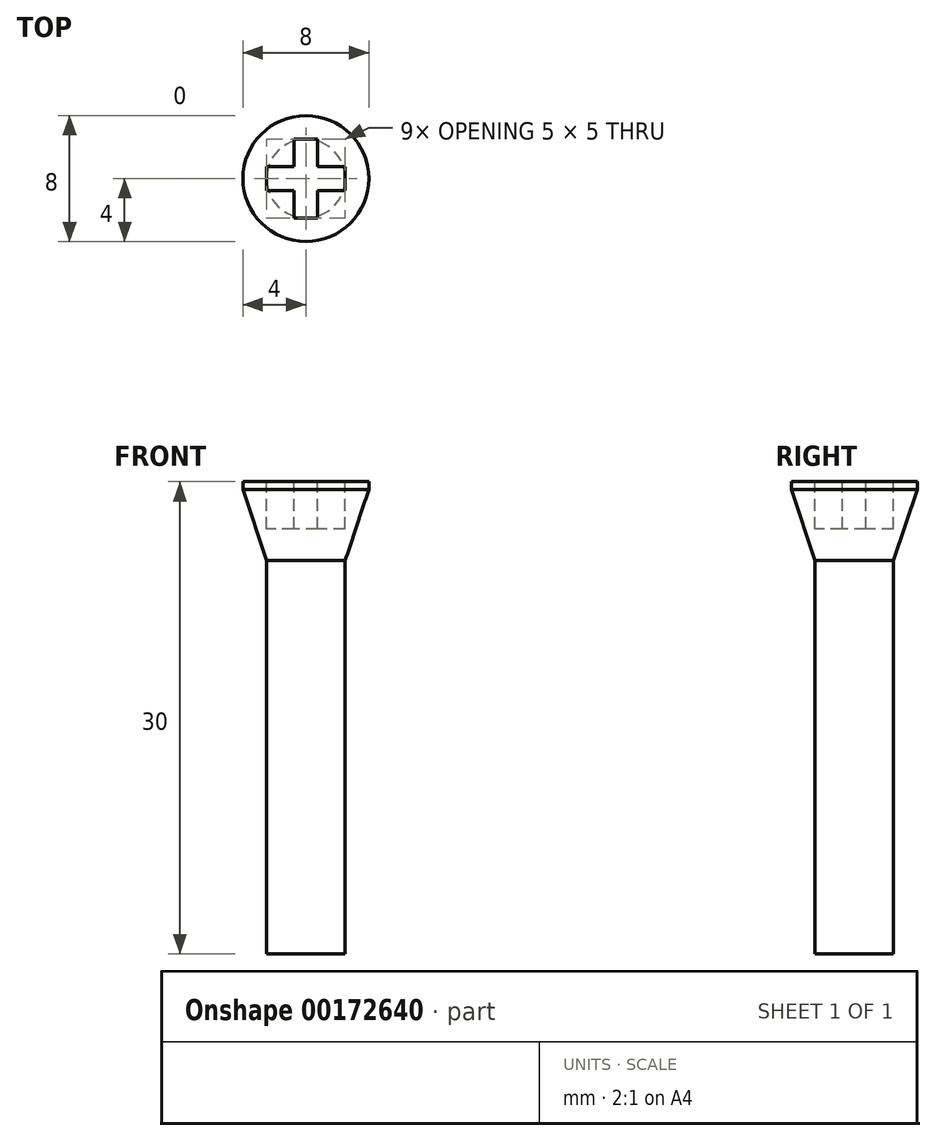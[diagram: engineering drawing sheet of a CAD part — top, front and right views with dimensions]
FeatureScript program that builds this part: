
annotation { "Feature Type Name" : "Feature", "Feature Type Description" : "" }
export const myFeature = defineFeature(function(context is Context, id is Id, definition is map)
    precondition{}
    {
        {
            var Q0;
            Q0=qCreatedBy(makeId("Top.planeOp"),FACE);
            var sketch = newSketch(context, id + "F0", { "sketchPlane" : qUnion([Q0])});
            skCircle(sketch, "E0", {"center": v(0, 0) * mm, "radius": 4 * mm});
            skSolve(sketch);
        }
        {
            var Q0;
            Q0=qSketchRegion(id+"F0",true);
            extrude(context, id + "F1", {"entities" : qUnion([Q0]), "depth" : 5 * mm});
        }
        {
            var Q0;
            Q0=makeQuery(id+"F1.opExtrude","CAP_FACE",FACE,{"disambiguationData":[OSD([sQuery(id+"F0.wireOp",EDGE,"E0")])],"isStart":false});
            var sketch = newSketch(context, id + "F2", { "sketchPlane" : qUnion([Q0])});
            skCircle(sketch, "E1", {"center": v(0, 0) * mm, "radius": 2.5 * mm});
            skSolve(sketch);
        }
        {
            var Q0;
            Q0=qSketchRegion(id+"F2",true);
            extrude(context, id + "F3", {"entities" : qUnion([Q0]), "operationType" : NewBodyOperationType.ADD, "depth" : 25 * mm});
        }
        {
            var Q0;
            Q0=qCreatedBy(makeId("Front.planeOp"),FACE);
            var sketch = newSketch(context, id + "F4", { "sketchPlane" : qUnion([Q0])});
            skPoint(sketch, "E2", {"position": v(0, 5) * mm});
            skPoint(sketch, "E3", {"position": v(-4, 5) * mm});
            skPoint(sketch, "E4", {"position": v(-4, 0) * mm});
            skPoint(sketch, "E5", {"position": v(-4, 0.5) * mm});
            skPoint(sketch, "E6", {"position": v(-2.5, 5) * mm});
            skLineSegment(sketch, "E7", {"start": v(-2.5, 5) * mm, "end": v(-4, 0.5) * mm});
            skLineSegment(sketch, "E8", {"start": v(-4, 0.5) * mm, "end": v(-4, 5) * mm});
            skLineSegment(sketch, "E9", {"start": v(-2.5, 5) * mm, "end": v(-4, 5) * mm});
            skLineSegment(sketch, "E10", {"start": v(0, 5) * mm, "end": v(0, 0) * mm});
            skSolve(sketch);
        }
        {
            var Q0;
            Q0=qSketchRegion(id+"F4",true);
            var Q1;
            Q1=sQuery(id+"F4.wireOp",EDGE,"E10");
            revolve(context, id + "F5", {"operationType" : NewBodyOperationType.REMOVE, "entities" : qUnion([Q0]), "axis" : qUnion([Q1]), "revolveType" : RevolveType.FULL});
        }
        {
            var Q0;
            Q0=makeQuery(id+"F1.opExtrude","CAP_FACE",FACE,{"disambiguationData":[OSD([sQuery(id+"F0.wireOp",EDGE,"E0")])],"isStart":true});
            var sketch = newSketch(context, id + "F6", { "sketchPlane" : qUnion([Q0])});
            skLineSegment(sketch, "E11.bottom", {"start": v(2.5, 0.75) * mm, "end": v(-2.5, 0.75) * mm});
            skLineSegment(sketch, "E11.top", {"start": v(2.5, -0.75) * mm, "end": v(-2.5, -0.75) * mm});
            skLineSegment(sketch, "E11.left", {"start": v(2.5, 0.75) * mm, "end": v(2.5, -0.75) * mm});
            skLineSegment(sketch, "E11.right", {"start": v(-2.5, 0.75) * mm, "end": v(-2.5, -0.75) * mm});
            skPoint(sketch, "E11.middle", {"position": v(0, 0) * mm});
            skLineSegment(sketch, "E12.bottom", {"start": v(0.75, 2.5) * mm, "end": v(-0.75, 2.5) * mm});
            skLineSegment(sketch, "E12.top", {"start": v(0.75, -2.5) * mm, "end": v(-0.75, -2.5) * mm});
            skLineSegment(sketch, "E12.left", {"start": v(0.75, 2.5) * mm, "end": v(0.75, -2.5) * mm});
            skLineSegment(sketch, "E12.right", {"start": v(-0.75, 2.5) * mm, "end": v(-0.75, -2.5) * mm});
            skSolve(sketch);
        }
        {
            var Q0;
            Q0=qSketchRegion(id+"F6",true);
            extrude(context, id + "F7", {"entities" : qUnion([Q0]), "operationType" : NewBodyOperationType.REMOVE, "oppositeDirection" : true, "depth" : 3 * mm});
        }
        {
            var Q0;
            Q0=qCreatedBy(makeId("Front.planeOp"),FACE);
            var sketch = newSketch(context, id + "F8", { "sketchPlane" : qUnion([Q0])});
            skLineSegment(sketch, "E13", {"start": v(-47.34, 0) * mm, "end": v(66.67, 0) * mm, "construction": true});
            skSolve(sketch);
        }
        {
            var Q0;
            Q0=makeQuery(id+"F1.opExtrude","SWEPT_BODY",BODY,{"disambiguationData":[OSD([sQuery(id+"F0.wireOp",EDGE,"E0")])]});
            var Q1;
            Q1=sQuery(id+"F8.wireOp",EDGE,"E13");
            transform(context, id + "F9", {"entities" : qUnion([Q0]), "transformType" : TransformType.ROTATION, "transformAxis" : qUnion([Q1]), "angle" : 180 * degree, "makeCopy" : false});
        }
    });
